# Revit family: Mittel- und Feinschutz für Doppeladersysteme, Typ_ FRD, FLD
name_source: partatom
category: Generic Models
revit_build: Autodesk Revit 2015 (Build: 20140606_1530(x64)
units: mm (PartAtom-declared; Revit-internal decimal feet)

## types (16) — shared parameters
Cut depth = 12 mm  [stored 0.0393701 ft]
Height = 61 mm
Length = 18 mm
Manufacturer = OBO Bettermann
Material = OBO PA 6 GF20
Material 2 = OBO PE
URL = http://www.obo-bettermann.com
Width = 90 mm  [stored 0.295276 ft]

## per-type parameters (varying)
| type | GTIN | Manufacturer Art.No. |
| FRD 5 | 4012195578284 | 5098492 |
| FRD 12 | 4012195578291 | 5098506 |
| FRD 24 | 4012195578307 | 5098514 |
| FRD 48 | 4012195578314 | 5098522 |
| FRD 110 | 4012195578338 | 5098557 |
| FRD 2-24 | 4012195578420 | 5098727 |
| FLD 5 | 4012195578369 | 5098600 |
| FLD 12 | 4012195578376 | 5098603 |
| FLD 24 | 4012195578383 | 5098611 |
| FLD 48 | 4012195578390 | 5098630 |
| FLD 60 | 4012195578406 | 5098638 |
| FLD 110 | 4012195578413 | 5098646 |
| FLD 2-5 | 4012195578529 | 5098867 |
| FLD 2-12 | 4012195578444 | 5098808 |
| FLD 2-24 | 4012195578451 | 5098816 |
| FLD 2-110 | 4012195578512 | 5098859 |

note: column(s) folded — value = type name in every type: Article Type

note: [stored X ft] marks values corroborated as IEEE doubles in the binary element streams (Revit-internal decimal feet)

## geometry (parser evidence)
native form markers: Sweep x2
no freeform markers — native parametric forms only
